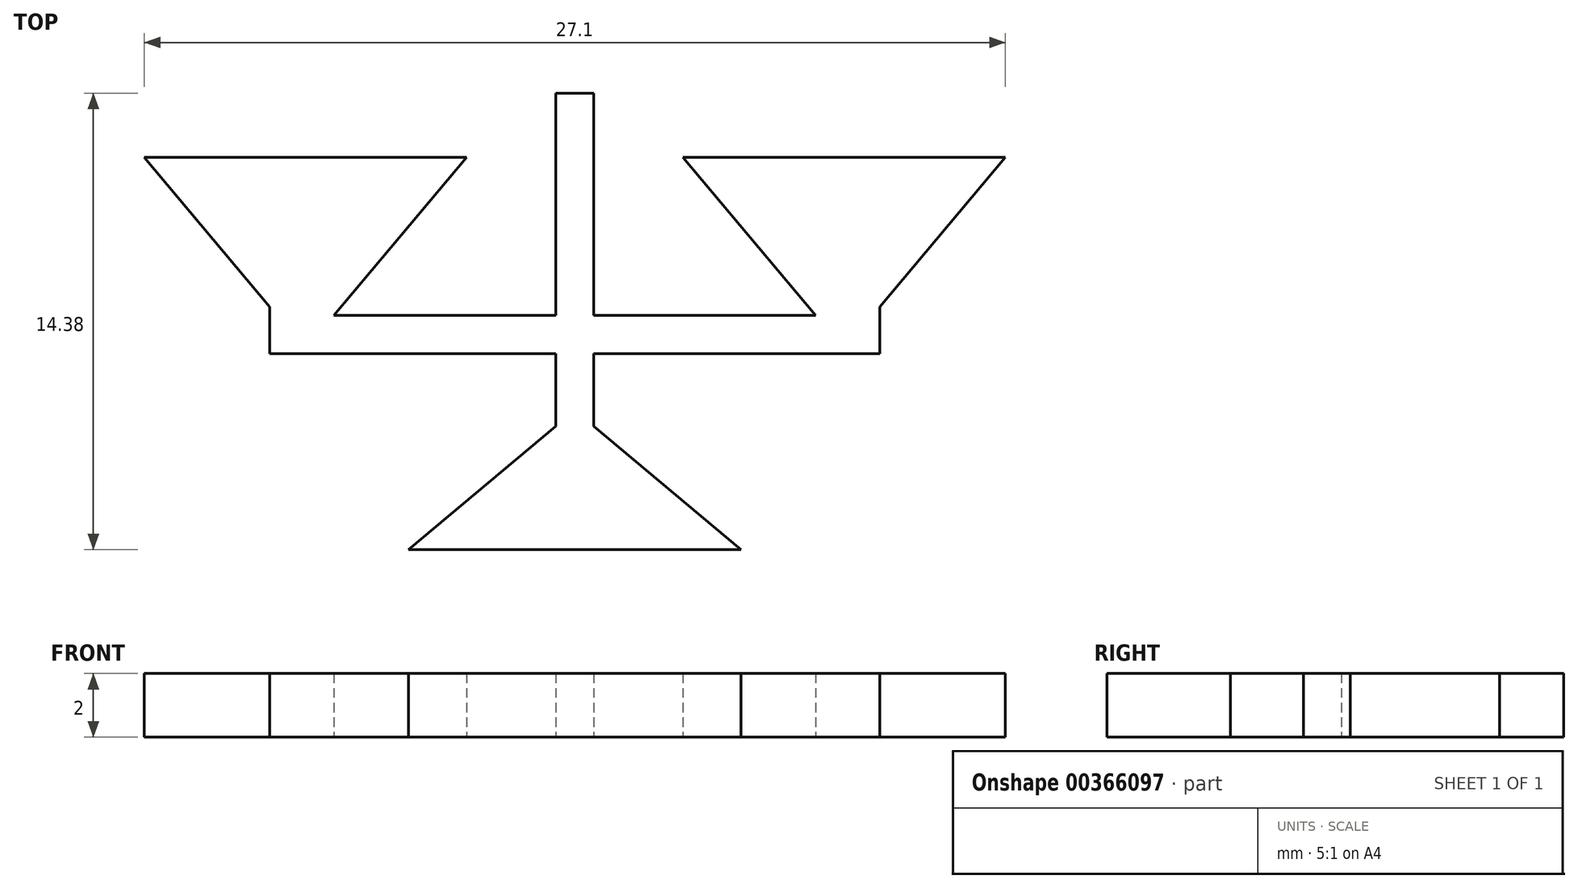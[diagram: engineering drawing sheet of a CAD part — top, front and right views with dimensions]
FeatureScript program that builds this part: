
annotation { "Feature Type Name" : "Feature", "Feature Type Description" : "" }
export const myFeature = defineFeature(function(context is Context, id is Id, definition is map)
    precondition{}
    {
        {
            var Q0;
            Q0=qCreatedBy(makeId("Top.planeOp"),FACE);
            var sketch = newSketch(context, id + "F0", { "sketchPlane" : qUnion([Q0])});
            skLineSegment(sketch, "E0", {"start": v(0, -11.75) * mm, "end": v(0, 20.53) * mm, "construction": true});
            skLineSegment(sketch, "E1", {"start": v(0, 7) * mm, "end": v(0.8, 7) * mm});
            skLineSegment(sketch, "E2", {"start": v(0.8, 7) * mm, "end": v(0.8, 0) * mm});
            skLineSegment(sketch, "E3", {"start": v(0.8, 0) * mm, "end": v(7.16, 0) * mm});
            skLineSegment(sketch, "E4", {"start": v(7.16, 0) * mm, "end": v(2.98, 4.98) * mm});
            skLineSegment(sketch, "E5", {"start": v(2.98, 4.98) * mm, "end": v(13.98, 4.98) * mm});
            skLineSegment(sketch, "E6", {"start": v(13.98, 4.98) * mm, "end": v(9.8, 0) * mm});
            skLineSegment(sketch, "E7", {"start": v(9.8, 0) * mm, "end": v(9.8, -1.6) * mm});
            skLineSegment(sketch, "E8", {"start": v(9.8, -1.6) * mm, "end": v(0.8, -1.6) * mm});
            skLineSegment(sketch, "E9", {"start": v(0.8, -1.6) * mm, "end": v(0.8, -3.6) * mm});
            skLineSegment(sketch, "E10", {"start": v(0.8, -3.6) * mm, "end": v(5.78, -7.78) * mm});
            skLineSegment(sketch, "E11", {"start": v(5.78, -7.78) * mm, "end": v(0, -7.78) * mm});
            skLineSegment(sketch, "E12", {"start": v(8.48, 4.98) * mm, "end": v(8.48, 0) * mm, "construction": true});
            skLineSegment(sketch, "E13.MirrorCS", {"start": v(0, 7) * mm, "end": v(-0.8, 7) * mm});
            skLineSegment(sketch, "E14.MirrorCS", {"start": v(-9.8, 0) * mm, "end": v(-9.8, -1.6) * mm});
            skLineSegment(sketch, "E15.MirrorCS", {"start": v(-0.8, 7) * mm, "end": v(-0.8, 0) * mm});
            skLineSegment(sketch, "E16.MirrorCS", {"start": v(-0.8, 0) * mm, "end": v(-7.16, 0) * mm});
            skLineSegment(sketch, "E17.MirrorCS", {"start": v(-7.16, 0) * mm, "end": v(-2.98, 4.98) * mm});
            skLineSegment(sketch, "E18.MirrorCS", {"start": v(-2.98, 4.98) * mm, "end": v(-13.98, 4.98) * mm});
            skLineSegment(sketch, "E19.MirrorCS", {"start": v(-13.98, 4.98) * mm, "end": v(-9.8, 0) * mm});
            skLineSegment(sketch, "E20.MirrorCS", {"start": v(-9.8, -1.6) * mm, "end": v(-0.8, -1.6) * mm});
            skLineSegment(sketch, "E21.MirrorCS", {"start": v(-0.8, -1.6) * mm, "end": v(-0.8, -3.6) * mm});
            skLineSegment(sketch, "E22.MirrorCS", {"start": v(-0.8, -3.6) * mm, "end": v(-5.78, -7.78) * mm});
            skLineSegment(sketch, "E23.MirrorCS", {"start": v(-5.78, -7.78) * mm, "end": v(0, -7.78) * mm});
            skLineSegment(sketch, "E24.0", {"start": v(-9.6, -1.4) * mm, "end": v(-0.6, -1.4) * mm});
            skLineSegment(sketch, "E24.1", {"start": v(-9.6, 0.07) * mm, "end": v(-9.6, -1.4) * mm});
            skLineSegment(sketch, "E24.2", {"start": v(-13.55, 4.78) * mm, "end": v(-9.6, 0.07) * mm});
            skLineSegment(sketch, "E24.3", {"start": v(-3.4, 4.78) * mm, "end": v(-13.55, 4.78) * mm});
            skLineSegment(sketch, "E24.4", {"start": v(-7.59, -0.2) * mm, "end": v(-3.4, 4.78) * mm});
            skLineSegment(sketch, "E24.5", {"start": v(-0.6, -1.4) * mm, "end": v(-0.6, -3.7) * mm});
            skLineSegment(sketch, "E24.6", {"start": v(-0.6, -0.2) * mm, "end": v(-7.59, -0.2) * mm});
            skLineSegment(sketch, "E24.7", {"start": v(-0.6, 6.8) * mm, "end": v(-0.6, -0.2) * mm});
            skLineSegment(sketch, "E24.8", {"start": v(0, 6.8) * mm, "end": v(-0.6, 6.8) * mm});
            skLineSegment(sketch, "E24.9", {"start": v(0, 6.8) * mm, "end": v(0.6, 6.8) * mm});
            skLineSegment(sketch, "E24.10", {"start": v(0.6, 6.8) * mm, "end": v(0.6, -0.2) * mm});
            skLineSegment(sketch, "E24.11", {"start": v(0.6, -0.2) * mm, "end": v(7.59, -0.2) * mm});
            skLineSegment(sketch, "E24.12", {"start": v(0.6, -3.7) * mm, "end": v(5.23, -7.58) * mm});
            skLineSegment(sketch, "E24.13", {"start": v(5.23, -7.58) * mm, "end": v(0, -7.58) * mm});
            skLineSegment(sketch, "E24.14", {"start": v(-5.23, -7.58) * mm, "end": v(0, -7.58) * mm});
            skLineSegment(sketch, "E24.15", {"start": v(-0.6, -3.7) * mm, "end": v(-5.23, -7.58) * mm});
            skLineSegment(sketch, "E24.16", {"start": v(0.6, -1.4) * mm, "end": v(0.6, -3.7) * mm});
            skLineSegment(sketch, "E24.17", {"start": v(9.6, -1.4) * mm, "end": v(0.6, -1.4) * mm});
            skLineSegment(sketch, "E24.18", {"start": v(9.6, 0.07) * mm, "end": v(9.6, -1.4) * mm});
            skLineSegment(sketch, "E24.19", {"start": v(13.55, 4.78) * mm, "end": v(9.6, 0.07) * mm});
            skLineSegment(sketch, "E24.20", {"start": v(3.4, 4.78) * mm, "end": v(13.55, 4.78) * mm});
            skLineSegment(sketch, "E24.21", {"start": v(7.59, -0.2) * mm, "end": v(3.4, 4.78) * mm});
            skSolve(sketch);
        }
        {
            var Q0;
            Q0=makeQuery(id+"F0.imprint","IMPRINT",FACE,{"disambiguationData":[TD([[makeQuery(id+"F0.imprint","IMPRINT",EDGE,{"derivedFrom":sQuery(id+"F0.wireOp",EDGE,"E24.0")}),1.0]])]});
            extrude(context, id + "F1", {"entities" : qUnion([Q0]), "depth" : 2 * mm});
        }
    });
